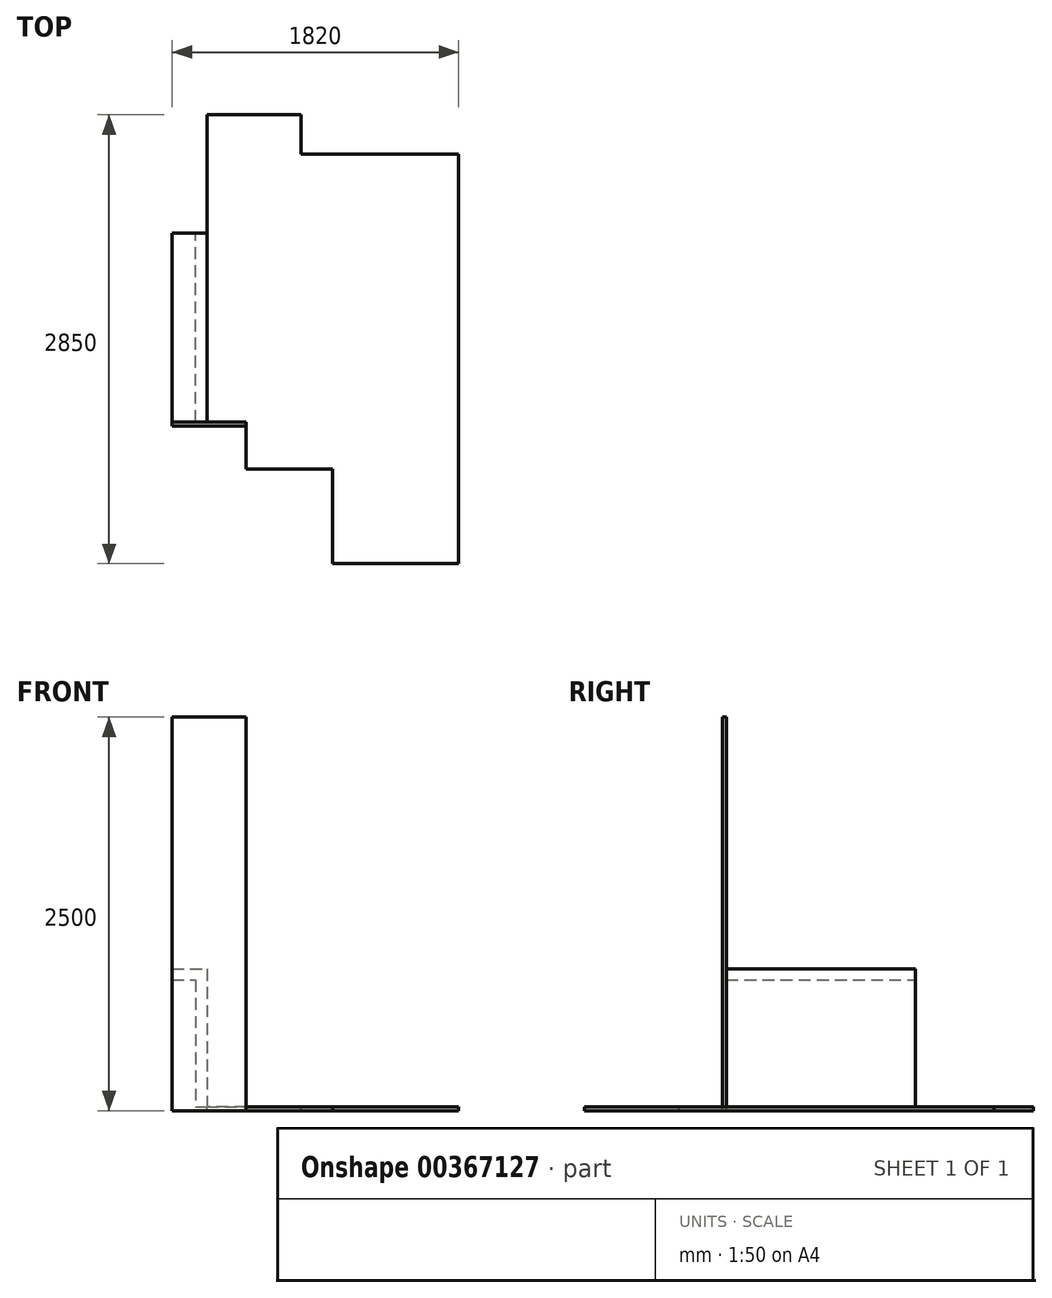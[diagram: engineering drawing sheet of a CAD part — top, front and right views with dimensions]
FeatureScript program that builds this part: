
annotation { "Feature Type Name" : "Feature", "Feature Type Description" : "" }
export const myFeature = defineFeature(function(context is Context, id is Id, definition is map)
    precondition{}
    {
        {
            var Q0;
            Q0=qCreatedBy(makeId("Top.planeOp"),FACE);
            var sketch = newSketch(context, id + "F0", { "sketchPlane" : qUnion([Q0])});
            skLineSegment(sketch, "E0", {"start": v(0, 0) * mm, "end": v(0, -2600) * mm});
            skLineSegment(sketch, "E1", {"start": v(0, -2600) * mm, "end": v(-800, -2600) * mm});
            skLineSegment(sketch, "E2", {"start": v(-800, -2600) * mm, "end": v(-800, -2000) * mm});
            skLineSegment(sketch, "E3", {"start": v(-800, -2000) * mm, "end": v(-1350, -2000) * mm});
            skLineSegment(sketch, "E4", {"start": v(-1350, -2000) * mm, "end": v(-1350, -1700) * mm});
            skLineSegment(sketch, "E5", {"start": v(-1350, -1700) * mm, "end": v(-1600, -1700) * mm});
            skLineSegment(sketch, "E6", {"start": v(-1600, -1700) * mm, "end": v(-1600, 250) * mm});
            skLineSegment(sketch, "E7", {"start": v(-1600, 250) * mm, "end": v(-1000, 250) * mm});
            skLineSegment(sketch, "E8", {"start": v(-1000, 250) * mm, "end": v(-1000, 0) * mm});
            skLineSegment(sketch, "E9", {"start": v(-1000, 0) * mm, "end": v(0, 0) * mm});
            skSolve(sketch);
        }
        {
            var Q0;
            Q0 = qSketchRegion(id + "F0", true);
            extrude(context, id + "F1", {"entities" : qUnion([Q0]), "oppositeDirection" : true, "depth" : 25 * mm});
        }
        {
            var Q0;
            Q0=makeQuery(id+"F1.opExtrude","SWEPT_FACE",FACE,{"disambiguationData":[OSD([sQuery(id+"F0.wireOp",EDGE,"E6")])]});
            var sketch = newSketch(context, id + "F2", { "sketchPlane" : qUnion([Q0])});
            skLineSegment(sketch, "E10.bottom", {"start": v(500, 875) * mm, "end": v(1700, 875) * mm});
            skLineSegment(sketch, "E10.top", {"start": v(500, -25) * mm, "end": v(1700, -25) * mm});
            skLineSegment(sketch, "E10.left", {"start": v(500, 875) * mm, "end": v(500, -25) * mm});
            skLineSegment(sketch, "E10.right", {"start": v(1700, 875) * mm, "end": v(1700, -25) * mm});
            skSolve(sketch);
        }
        {
            var Q0;
            {var subQ0=sQuery(id+"F2.wireOp",EDGE,"E10.bottom");Q0=makeQuery(id+"F2.imprint","IMPRINT",FACE,{"disambiguationData":[TD([[makeQuery(id+"F2.imprint","IMPRINT",EDGE,{"derivedFrom":subQ0}),-1.0]])]});}
            extrude(context, id + "F3", {"entities" : qUnion([Q0]), "depth" : 70 * mm});
        }
        {
            var Q0;
            Q0=makeQuery(id+"F3.opExtrude","CAP_FACE",FACE,{"disambiguationData":[OSD([sQuery(id+"F0.wireOp",EDGE,"E6"),sQuery(id+"F2.wireOp",EDGE,"E10.bottom"),sQuery(id+"F2.wireOp",EDGE,"E10.left"),sQuery(id+"F2.wireOp",EDGE,"E10.right")])],"isStart":false});
            var sketch = newSketch(context, id + "F4", { "sketchPlane" : qUnion([Q0])});
            skLineSegment(sketch, "E11.bottom", {"start": v(1700, 798.23) * mm, "end": v(1700, 798.23) * mm});
            skLineSegment(sketch, "E11.top", {"start": v(1700, 875) * mm, "end": v(1700, 875) * mm});
            skLineSegment(sketch, "E11.left", {"start": v(1700, 798.23) * mm, "end": v(1700, 875) * mm});
            skLineSegment(sketch, "E11.right", {"start": v(1700, 798.23) * mm, "end": v(1700, 875) * mm});
            skLineSegment(sketch, "E12.bottom", {"start": v(1700, 875) * mm, "end": v(500, 875) * mm});
            skLineSegment(sketch, "E12.top", {"start": v(1700, 805) * mm, "end": v(500, 805) * mm});
            skLineSegment(sketch, "E12.left", {"start": v(1700, 875) * mm, "end": v(1700, 805) * mm});
            skLineSegment(sketch, "E12.right", {"start": v(500, 875) * mm, "end": v(500, 805) * mm});
            skSolve(sketch);
        }
        {
            var Q0;
            Q0=makeQuery(id+"F4.imprint","IMPRINT",FACE,{"disambiguationData":[TD([[makeQuery(id+"F4.imprint","IMPRINT",EDGE,{"derivedFrom":sQuery(id+"F4.wireOp",EDGE,"E12.bottom")}),-1.0]])]});
            extrude(context, id + "F5", {"entities" : qUnion([Q0]), "operationType" : NewBodyOperationType.ADD, "depth" : 150 * mm});
        }
        {
            var Q0;
            Q0=makeQuery(id+"F1.opExtrude","SWEPT_FACE",FACE,{"disambiguationData":[OSD([sQuery(id+"F0.wireOp",EDGE,"E5")])]});
            var sketch = newSketch(context, id + "F6", { "sketchPlane" : qUnion([Q0])});
            skLineSegment(sketch, "E13.bottom", {"start": v(-1350, -25) * mm, "end": v(-1820, -25) * mm});
            skLineSegment(sketch, "E13.top", {"start": v(-1350, 2475) * mm, "end": v(-1820, 2475) * mm});
            skLineSegment(sketch, "E13.left", {"start": v(-1350, -25) * mm, "end": v(-1350, 2475) * mm});
            skLineSegment(sketch, "E13.right", {"start": v(-1820, -25) * mm, "end": v(-1820, 2475) * mm});
            skSolve(sketch);
        }
        {
            var Q0;
            {var subQ4=sQuery(id+"F6.wireOp",EDGE,"E13.top");Q0=makeQuery(id+"F6.imprint","IMPRINT",FACE,{"disambiguationData":[TD([[makeQuery(id+"F6.imprint","IMPRINT",EDGE,{"derivedFrom":subQ4}),1.0]])]});}
            var Q1;
            {var subQ3=sQuery(id+"F0.wireOp",EDGE,"E5");var subQ5=makeQuery(id+"F1.opExtrude","CAP_EDGE",EDGE,{"disambiguationData":[OSD([subQ3])],"isStart":true});Q1=makeQuery(id+"F6.imprint","IMPRINT",FACE,{"disambiguationData":[TD([[makeQuery(id+"F6.imprint","IMPRINT",EDGE,{"derivedFrom":subQ5}),1.0]])]});}
            extrude(context, id + "F7", {"entities" : qUnion([Q0, Q1]), "depth" : 25 * mm});
        }
    });
